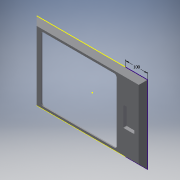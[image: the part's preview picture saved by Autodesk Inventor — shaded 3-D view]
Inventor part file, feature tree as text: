
AUTODESK INVENTOR PART (.ipt)
format: ipt  version: 2018 (Build 220112000, 112)  size: 188,928 bytes
history: native  units: mm
features: sketch x6, extrude x5, projected_geometry x3, chamfer x1, fillet x1
ambient origin geometry x8: Origin, YZ Plane, XZ Plane, XY Plane, X Axis, Y Axis, Z Axis, Center Point
bodies: Volumenkörper1 (feature_tree)
feature tree (16):
  extrude  "Extrusion1"  Depth=20.0mm
  chamfer  "Fase1"  Distance=20.0mm
  sketch  "Skizze2"  dims[d4=20.0mm d5=2.0mm d6=45.0deg d7=100.0mm]
  extrude  "Extrusion6"  Depth=20.0mm
  extrude  "Extrusion5"  Depth=90.0mm
  fillet  "Rundung1"  Radius=20.0mm
  extrude  "Extrusion7"  Depth=4.0mm
  extrude  "Extrusion8"  Depth=20.0mm
  sketch  "Skizze1"  dims[d0=400.0mm d1=500.0mm d2=20.0mm d3=0.0mm]
  sketch  "Skizze6"  dims[d23=50.0mm d24=90.0mm d25=20.0mm]
  sketch  "Skizze7"  dims[d26=15.0mm d27=0.0mm d28=4.0mm]
  projected_geometry  "Projizierte Kontur2"
  sketch  "Skizze8"  dims[d35=380.0mm d37=20.0mm]
  projected_geometry  "Projizierte Kontur3"
  sketch  "Skizze9"  dims[d38=20.0mm d39=10.0mm d40=0.0mm d41=10.0mm d43=10.0mm d45=10.0mm d46=10.0mm d47=5.0mm d48=0.0mm d49=10.0mm d50=5.0mm d51=0.0mm d53=20.0mm d54=10.0mm d57=10.0mm]
  projected_geometry  "Projizierte Kontur4"
